# Revit family: OBN_Wall
name_source: partatom
category: Lighting Fixtures
revit_build: Autodesk Revit 2014 (Build: 20130308_1515(x64)
units: mm (PartAtom-declared; Revit-internal decimal feet)

## types (1)
- OBN
    Apparent Load = 4 VA
    Application = The Sempra® MR Series are a set of compact, low-profile Master/
Remote exit sign featuring cast aluminum construction. It allows for
easy installation and has energy saving, long-life LED lamps.
    Certification = UL 924 Listed
NFPA 101 Life Safety Code
CEC T20 Compliant
    Default Elevation = 48.000"
    Description = The CLS Series offers bright and even LED EXIT or STAIRS glass panel illumination with Red letters, white LED's and a 20 gauge, durable steel housing. Features include AC or Emergency operation in single or double face. 120/277 VAC input. City of Chicago approved.
    Features = Improved one-piece design in AC or emergency operation
Highly reliable and energy efficient LED illumination
Long lasting Nickel Cadmium Battery
Glass panels with EXIT or STAIRS
    Finish = Hubbell - White
    Glass = Hubbell - light Glass
    Holder Material = Hubbell - Steel
    Lamp = LED Lamp
    Lens = Hubbell - Red Glass
    Load Classification = Lighting
    Manufacturer = DUAL-LITE
    Model = CLS
    Product Documentation Link = https://hubbellcdn.com
    Product Page URL = https://www.hubbell.com
    Type Comments = Exit Light
    URL = https://www.hubbell.com
    Wall Plate Material = Plastic, Opaque White
    Warranty = Fixture: 5 Years Full; Battery: 2 Years Full, 8 Years Pro-Rata
    Wattage Comments = 3.72 W
    Watts = 4 W

## geometry (parser evidence)
native form markers: Blend x8, Sweep x4
no freeform markers — native parametric forms only
